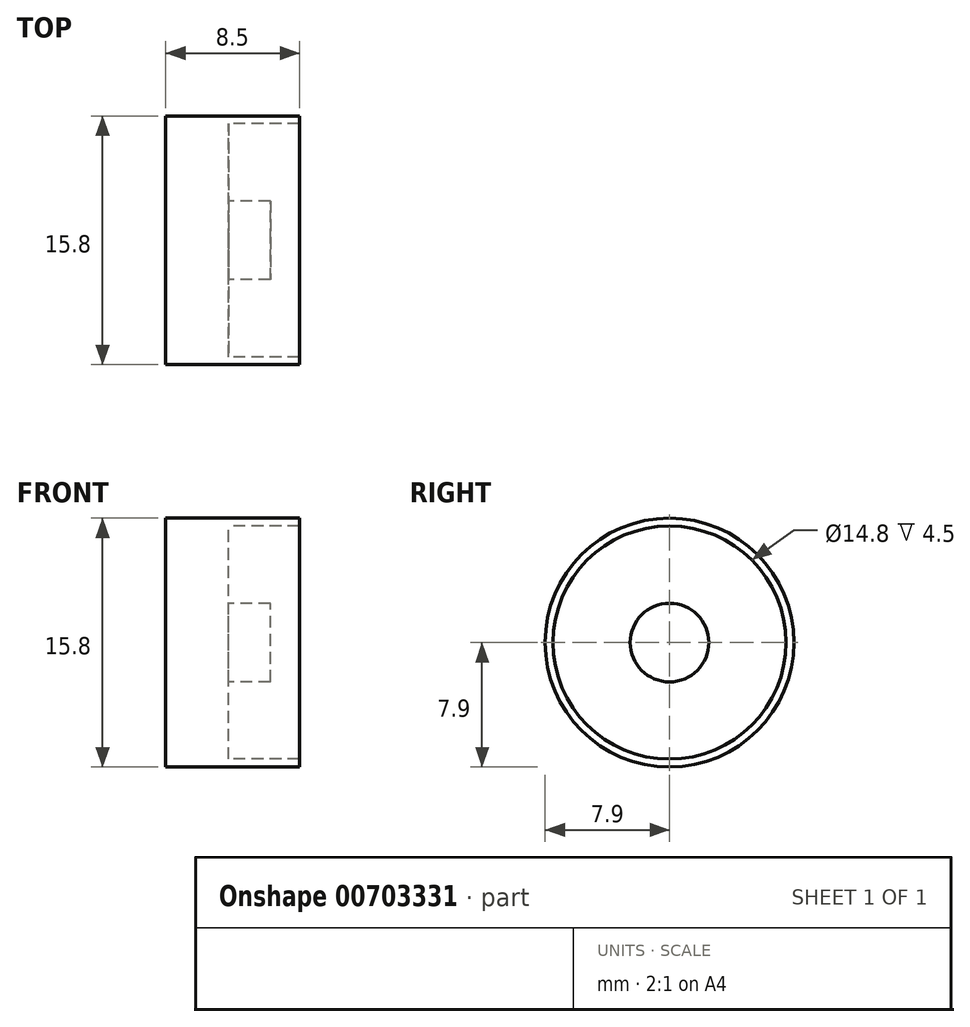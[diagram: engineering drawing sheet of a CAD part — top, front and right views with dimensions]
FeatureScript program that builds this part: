
annotation { "Feature Type Name" : "Feature", "Feature Type Description" : "" }
export const myFeature = defineFeature(function(context is Context, id is Id, definition is map)
    precondition{}
    {
        {
            var Q0;
            Q0=qCreatedBy(makeId("Right.planeOp"),FACE);
            var sketch = newSketch(context, id + "F0", { "sketchPlane" : qUnion([Q0])});
            skCircle(sketch, "E0", {"center": v(0, 0) * mm, "radius": 7.9 * mm});
            skCircle(sketch, "E1", {"center": v(0, 0) * mm, "radius": 7.4 * mm});
            skCircle(sketch, "E2", {"center": v(0, 0) * mm, "radius": 2.5 * mm});
            skSolve(sketch);
        }
        {
            var Q0;
            Q0=makeQuery(id+"F0.imprint","IMPRINT",FACE,{"disambiguationData":[TD([[makeQuery(id+"F0.imprint","IMPRINT",EDGE,{"derivedFrom":sQuery(id+"F0.wireOp",EDGE,"E1")}),1.0]])]});
            extrude(context, id + "F1", {"entities" : qUnion([Q0]), "depth" : 4 * mm, "offsetDistance" : 25 * mm});
        }
        {
            var Q0;
            Q0=makeQuery(id+"F0.imprint","IMPRINT",FACE,{"disambiguationData":[TD([[makeQuery(id+"F0.imprint","IMPRINT",EDGE,{"derivedFrom":sQuery(id+"F0.wireOp",EDGE,"E0")}),1.0]])]});
            extrude(context, id + "F2", {"entities" : qUnion([Q0]), "operationType" : NewBodyOperationType.ADD, "depth" : 8.5 * mm, "offsetDistance" : 25 * mm});
        }
        {
            var Q0;
            Q0=makeQuery(id+"F0.imprint","IMPRINT",FACE,{"disambiguationData":[TD([[makeQuery(id+"F0.imprint","IMPRINT",EDGE,{"derivedFrom":sQuery(id+"F0.wireOp",EDGE,"E2")}),1.0]])]});
            extrude(context, id + "F3", {"entities" : qUnion([Q0]), "operationType" : NewBodyOperationType.ADD, "depth" : 6.65 * mm, "offsetDistance" : 25 * mm});
        }
    });
